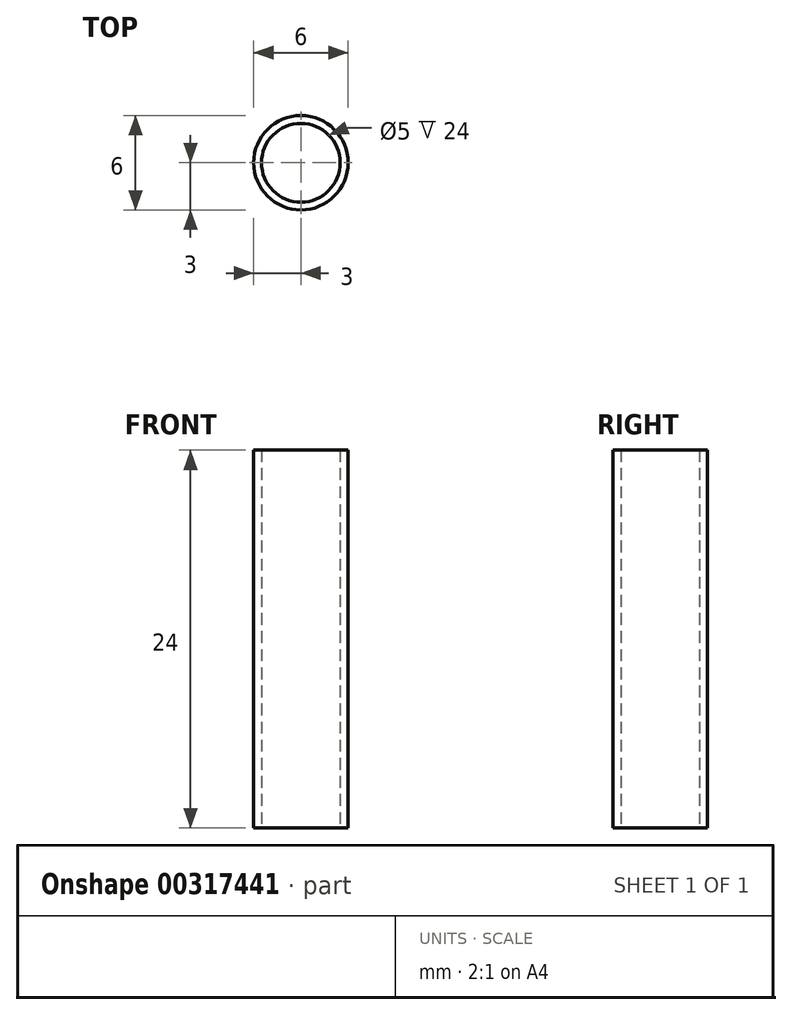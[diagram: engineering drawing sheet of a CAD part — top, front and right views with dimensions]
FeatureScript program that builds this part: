
annotation { "Feature Type Name" : "Feature", "Feature Type Description" : "" }
export const myFeature = defineFeature(function(context is Context, id is Id, definition is map)
    precondition{}
    {
        {
            var Q0;
            Q0=qCreatedBy(makeId("Top.planeOp"),FACE);
            var sketch = newSketch(context, id + "F0", { "sketchPlane" : qUnion([Q0])});
            skLineSegment(sketch, "E0.rect.bottom", {"start": v(-28.11, 28.11) * mm, "end": v(28.12, 28.11) * mm});
            skLineSegment(sketch, "E0.rect.top", {"start": v(-28.11, -28.11) * mm, "end": v(28.11, -28.11) * mm});
            skLineSegment(sketch, "E0.rect.left", {"start": v(-28.11, 28.12) * mm, "end": v(-28.12, -28.11) * mm});
            skLineSegment(sketch, "E0.rect.right", {"start": v(28.12, 28.12) * mm, "end": v(28.11, -28.11) * mm});
            skPoint(sketch, "E0.rect.middle", {"position": v(0, 0) * mm});
            skCircle(sketch, "E1", {"center": v(0, 0) * mm, "radius": 19.04 * mm});
            skCircle(sketch, "E2", {"center": v(0, 0) * mm, "radius": 3.98 * mm});
            skCircle(sketch, "E3", {"center": v(-23.62, 23.62) * mm, "radius": 2.5 * mm});
            skCircle(sketch, "E4", {"center": v(23.62, 23.62) * mm, "radius": 2.5 * mm});
            skCircle(sketch, "E5", {"center": v(23.62, -23.62) * mm, "radius": 2.5 * mm});
            skCircle(sketch, "E6", {"center": v(-23.62, -23.62) * mm, "radius": 2.5 * mm});
            skLineSegment(sketch, "E7.rect.bottom", {"start": v(-23.62, 23.62) * mm, "end": v(23.62, 23.62) * mm, "construction": true});
            skLineSegment(sketch, "E7.rect.top", {"start": v(-23.62, -23.62) * mm, "end": v(23.62, -23.62) * mm, "construction": true});
            skLineSegment(sketch, "E7.rect.left", {"start": v(-23.62, 23.62) * mm, "end": v(-23.62, -23.62) * mm, "construction": true});
            skLineSegment(sketch, "E7.rect.right", {"start": v(23.62, 23.62) * mm, "end": v(23.62, -23.62) * mm, "construction": true});
            skCircle(sketch, "E8", {"center": v(0, 0) * mm, "radius": 5.38 * mm});
            skCircle(sketch, "E9", {"center": v(-25.37, 0) * mm, "radius": 8.13 * mm});
            skCircle(sketch, "E10", {"center": v(25.37, 0) * mm, "radius": 8.13 * mm});
            skCircle(sketch, "E11", {"center": v(0, -25.37) * mm, "radius": 8.13 * mm});
            skCircle(sketch, "E12", {"center": v(-25.37, 0) * mm, "radius": 3.42 * mm});
            skCircle(sketch, "E13", {"center": v(25.37, 0) * mm, "radius": 3.41 * mm});
            skCircle(sketch, "E14", {"center": v(0, -25.37) * mm, "radius": 3.42 * mm});
            skCircle(sketch, "E15", {"center": v(-23.62, 23.62) * mm, "radius": 3 * mm});
            skSolve(sketch);
        }
        {
            var Q0;
            Q0=makeQuery(id+"F0.imprint","IMPRINT",FACE,{"disambiguationData":[TD([[makeQuery(id+"F0.imprint","IMPRINT",EDGE,{"derivedFrom":sQuery(id+"F0.wireOp",EDGE,"E3")}),-1.0]])]});
            extrude(context, id + "F1", {"entities" : qUnion([Q0]), "offsetDistance" : 25 * mm, "depth" : 24 * mm});
        }
    });
